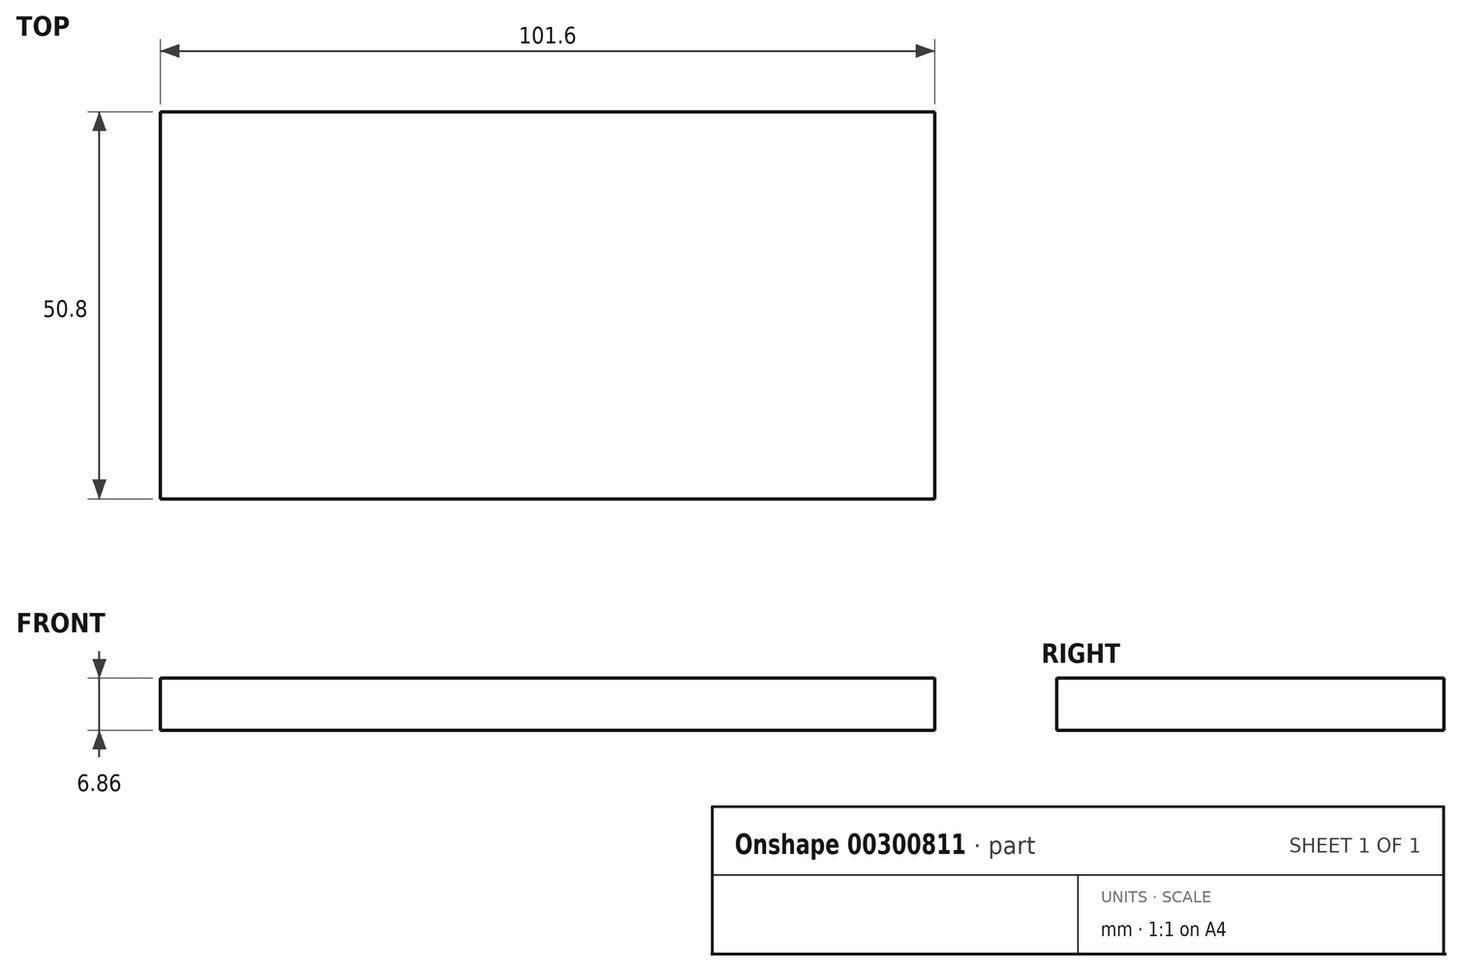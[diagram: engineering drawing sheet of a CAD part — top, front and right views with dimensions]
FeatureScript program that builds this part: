
annotation { "Feature Type Name" : "Feature", "Feature Type Description" : "" }
export const myFeature = defineFeature(function(context is Context, id is Id, definition is map)
    precondition{}
    {
        {
            var Q0;
            Q0=qCreatedBy(makeId("Top.planeOp"),FACE);
            var sketch = newSketch(context, id + "F0", { "sketchPlane" : qUnion([Q0])});
            skLineSegment(sketch, "E0.bottom", {"start": v(-92.52, 8.9) * mm, "end": v(9.08, 8.9) * mm});
            skLineSegment(sketch, "E0.top", {"start": v(-92.52, -41.9) * mm, "end": v(9.08, -41.9) * mm});
            skLineSegment(sketch, "E0.left", {"start": v(-92.52, 8.9) * mm, "end": v(-92.52, -41.9) * mm});
            skLineSegment(sketch, "E0.right", {"start": v(9.08, 8.9) * mm, "end": v(9.08, -41.9) * mm});
            skSolve(sketch);
        }
        {
            var Q0;
            Q0 = qSketchRegion(id + "F0", true);
            extrude(context, id + "F1", {"entities" : qUnion([Q0]), "depth" : 6.86 * mm});
        }
    });
